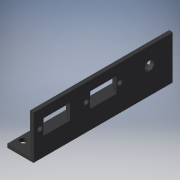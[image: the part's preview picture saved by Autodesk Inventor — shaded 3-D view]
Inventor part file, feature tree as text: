
AUTODESK INVENTOR PART (.ipt)
format: ipt  version: 2018 (Build 220112000, 112)  size: 155,136 bytes
history: native  units: in
note: dims shown in document units (in); Inventor stores cm internally (conversion verified against a paired STEP export)
features: sketch x3, extrude x3, projected_geometry x1
ambient origin geometry x8: Origin, YZ Plane, XZ Plane, XY Plane, X Axis, Y Axis, Z Axis, Center Point
bodies: Solid1 (feature_tree)
feature tree (7):
  sketch  "Sketch2"  dims[d0=0.75in d1=4.0in]
  extrude  "Extrusion3"  Depth=4.0in
  extrude  "Extrusion4"  Depth=0.3in
  extrude  "Extrusion5"  Depth=1.15in
  sketch  "Sketch4"  dims[d2=0.6in d3=0.3in]
  sketch  "Sketch5"  dims[d4=0.2in d10=0.6in d11=0.3in d12=0.2in d13=0.1in d14=0.0in d15=0.1in d16=4.0in d17=1.15in d18=0.0in d19=1.3333in d20=1.333in d21=0.5in d22=0.5in d23=0.5in d24=0.4823in d25=0.9646in d26=0.4823in d27=0.9646in d28=0.13in d29=0.13in d30=0.13in d31=0.13in d32=0.748in d33=0.4331in d34=0.748in d35=0.4331in d36=0.26in d37=1.15in d38=0.0in]
  projected_geometry  "Projected Loop1"
